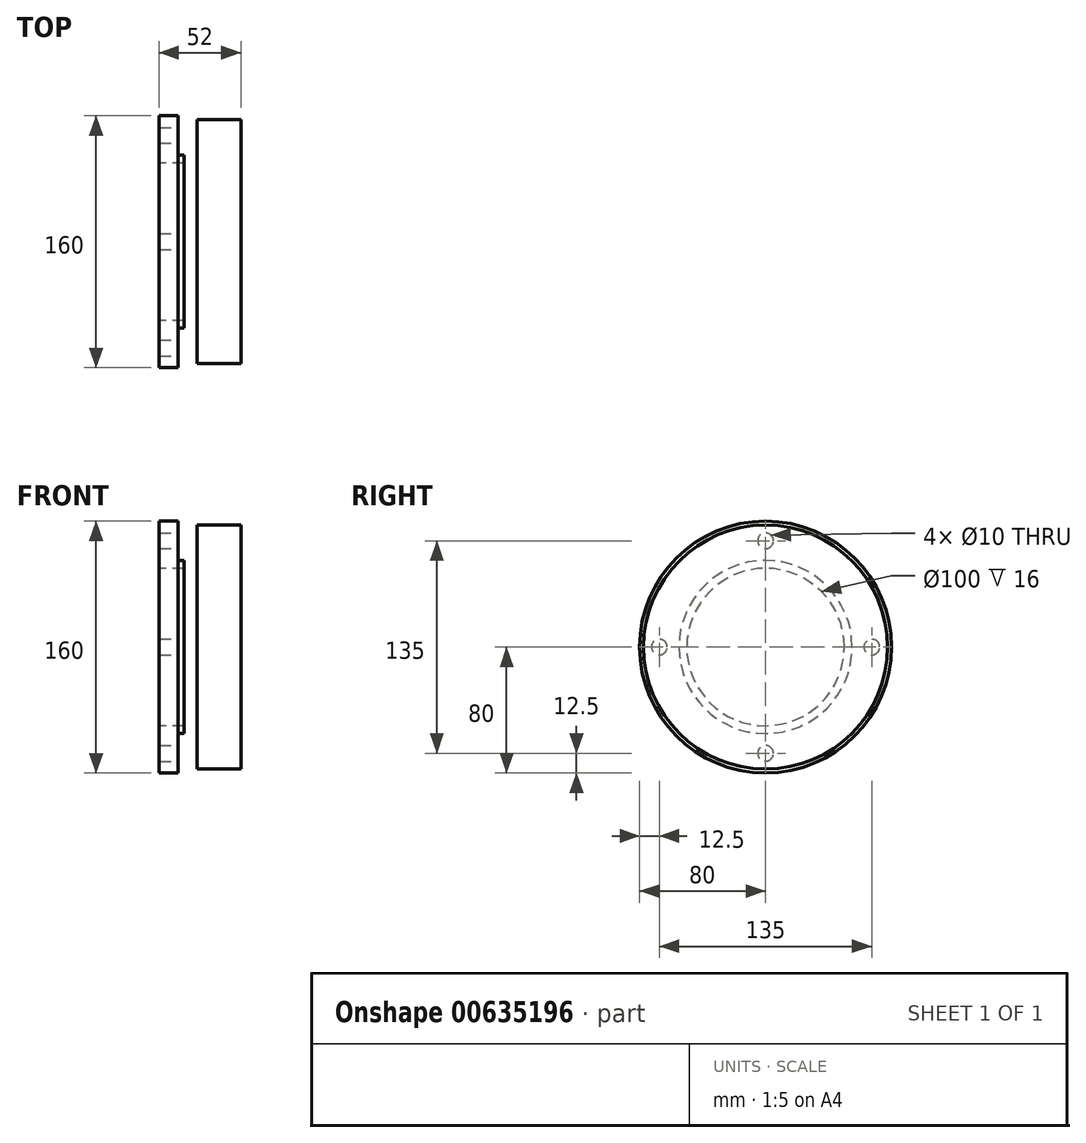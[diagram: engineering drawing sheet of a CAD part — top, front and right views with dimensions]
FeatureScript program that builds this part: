
annotation { "Feature Type Name" : "Feature", "Feature Type Description" : "" }
export const myFeature = defineFeature(function(context is Context, id is Id, definition is map)
    precondition{}
    {
        {
            var Q0;
            Q0=qCreatedBy(makeId("Right.planeOp"),FACE);
            var sketch = newSketch(context, id + "F0", { "sketchPlane" : qUnion([Q0])});
            skCircle(sketch, "E0", {"center": v(0, 0) * mm, "radius": 55 * mm});
            skCircle(sketch, "E1", {"center": v(0, 0) * mm, "radius": 80 * mm});
            skCircle(sketch, "E2", {"center": v(0, 0) * mm, "radius": 50 * mm});
            skCircle(sketch, "E3", {"center": v(67.5, 0) * mm, "radius": 5 * mm});
            skCircle(sketch, "E4.1.0", {"center": v(0, 67.5) * mm, "radius": 5 * mm});
            skCircle(sketch, "E4.2.0", {"center": v(-67.5, 0) * mm, "radius": 5 * mm});
            skCircle(sketch, "E4.3.0", {"center": v(0, -67.5) * mm, "radius": 5 * mm});
            skSolve(sketch);
        }
        {
            var Q0;
            Q0=makeQuery(id+"F0.imprint","IMPRINT",FACE,{"disambiguationData":[TD([[makeQuery(id+"F0.imprint","IMPRINT",EDGE,{"derivedFrom":sQuery(id+"F0.wireOp",EDGE,"E0")}),-1.0]])]});
            extrude(context, id + "F1", {"entities" : qUnion([Q0]), "oppositeDirection" : true, "depth" : 12 * mm, "offsetDistance" : 25 * mm});
        }
        {
            var Q0;
            Q0=makeQuery(id+"F0.imprint","IMPRINT",FACE,{"disambiguationData":[TD([[makeQuery(id+"F0.imprint","IMPRINT",EDGE,{"derivedFrom":sQuery(id+"F0.wireOp",EDGE,"E0")}),1.0]])]});
            extrude(context, id + "F2", {"entities" : qUnion([Q0]), "operationType" : NewBodyOperationType.ADD, "depth" : 4 * mm, "offsetDistance" : 25 * mm, "hasSecondDirection" : true, "secondDirectionOppositeDirection" : true, "secondDirectionDepth" : 12 * mm});
        }
        {
            var Q0;
            Q0=qCreatedBy(makeId("Right.planeOp"),FACE);
            var sketch = newSketch(context, id + "F3", { "sketchPlane" : qUnion([Q0])});
            skCircle(sketch, "E5", {"center": v(0, 0) * mm, "radius": 77.5 * mm});
            skSolve(sketch);
        }
        {
            var Q0;
            Q0 = qSketchRegion(id + "F3", true);
            extrude(context, id + "F4", {"entities" : qUnion([Q0]), "depth" : 40 * mm, "offsetDistance" : 25 * mm, "hasSecondDirection" : true, "secondDirectionOppositeDirection" : true, "secondDirectionDepth" : -12 * mm});
        }
    });
